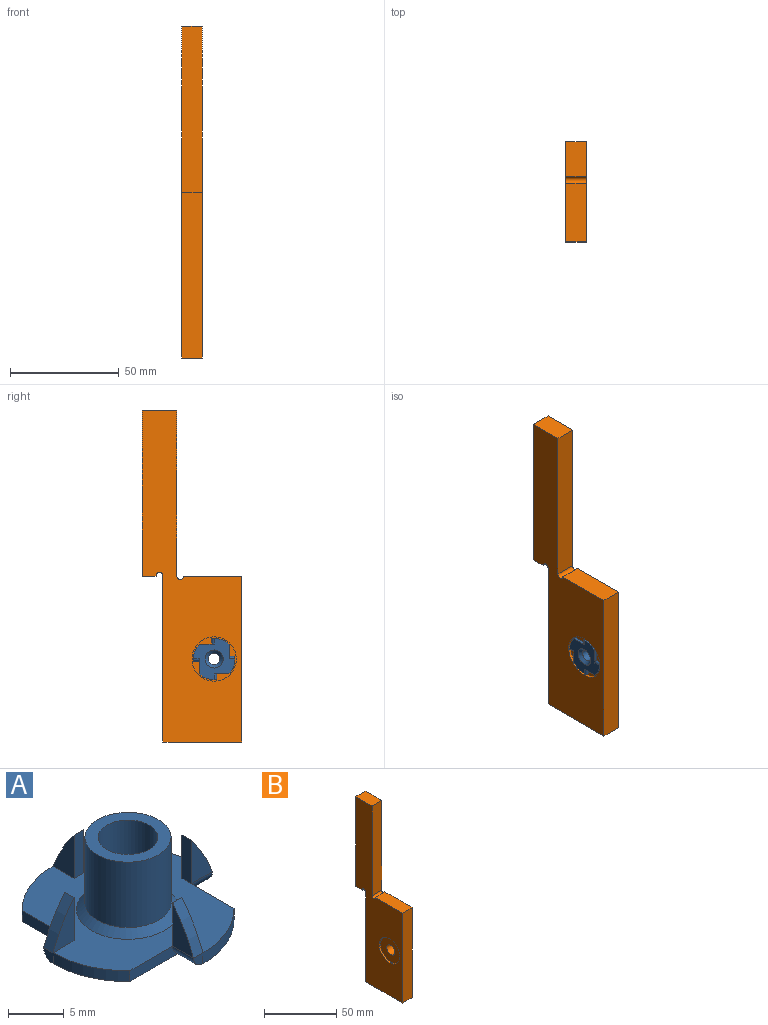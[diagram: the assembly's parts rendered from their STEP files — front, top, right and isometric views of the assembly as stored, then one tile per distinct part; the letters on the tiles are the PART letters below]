
ASSEMBLY  parts=2 mates=1
PART A: 39 faces, bbox 19.1x19.1x9.1 mm
  f0: cylinder r=9.53mm len=6.86mm, axis (0,0,-1), area 9.1mm2, adj f7,f10,f26,f28
  f1: cylinder r=16.73mm len=4.76mm, axis (0,-1,0), area 6.5mm2, adj f2,f3,f5,f6
  f2: plane 1.19x1.19mm, normal (1,0,0), area 1.1mm2, adj f1,f4,f27
  f3: plane 4.76x2.67mm, normal (0,-1,0), area 7.2mm2, adj f1,f4,f6
  f4: cylinder r=1.19mm len=2.67mm, axis (-1,0,0), area 5mm2, adj f2,f3,f7,f26
  f5: plane 4.76x2.67mm, normal (0,1,0), area 7.2mm2, adj f1,f6,f28
  f6: plane 4.76x1.19mm, normal (-1,0,0), area 5.7mm2, adj f1,f3,f5,f28
  f7: plane 6.61x1.19mm, normal (1,0,0), area 6.8mm2, adj f0,f4,f26,f28
  f8: cylinder r=9.53mm len=6.86mm, axis (0,0,-1), area 9.1mm2, adj f15,f18,f26,f28
  f9: cylinder r=16.73mm len=4.76mm, axis (-1,0,0), area 6.5mm2, adj f10,f11,f13,f14
  f10: plane 1.19x1.19mm, normal (0,-1,0), area 1.1mm2, adj f0,f9,f12
  f11: plane 4.76x2.67mm, normal (-1,0,0), area 7.2mm2, adj f9,f12,f14
  f12: cylinder r=1.19mm len=2.67mm, axis (0,1,0), area 5mm2, adj f10,f11,f15,f26
  f13: plane 4.76x2.67mm, normal (1,0,0), area 7.2mm2, adj f9,f14,f28
  f14: plane 4.76x1.19mm, normal (0,1,0), area 5.7mm2, adj f9,f11,f13,f28
  f15: plane 6.61x1.19mm, normal (0,-1,0), area 6.8mm2, adj f8,f12,f26,f28
  f16: cylinder r=9.53mm len=6.86mm, axis (0,0,-1), area 9.1mm2, adj f23,f26,f28,f34
  f17: cylinder r=16.73mm len=4.76mm, axis (0,1,0), area 6.5mm2, adj f18,f19,f21,f22
  f18: plane 1.19x1.19mm, normal (-1,0,0), area 1.1mm2, adj f8,f17,f20
  f19: plane 4.76x2.67mm, normal (0,1,0), area 7.2mm2, adj f17,f20,f22
  f20: cylinder r=1.19mm len=2.67mm, axis (1,0,0), area 5mm2, adj f18,f19,f23,f26
  f21: plane 4.76x2.67mm, normal (0,-1,0), area 7.2mm2, adj f17,f22,f28
  f22: plane 4.76x1.19mm, normal (1,0,0), area 5.7mm2, adj f17,f19,f21,f28
  f23: plane 6.61x1.19mm, normal (-1,0,0), area 6.8mm2, adj f16,f20,f26,f28
  f24: plane 4.76x2.67mm, normal (-1,0,0), area 7.2mm2, adj f28,f37,f38
  f25: cone r=2.68mm half-angle=45deg, axis (0,0,-1), area 44.3mm2, adj f26,f32
  f26: plane 19.05x19.05mm, normal (0,0,-1), area 182.6mm2, adj f0,f4,f7,f8,f12,f15,f16,f20
  f27: cylinder r=9.53mm len=6.86mm, axis (0,0,-1), area 9.1mm2, adj f2,f26,f28,f33
  f28: plane 19.05x19.05mm, normal (0,0,1), area 169mm2, adj f0,f5,f6,f7,f8,f13,f14,f15
  f29: cone r=4.64mm half-angle=45deg, axis (0,0,-1), area 28.8mm2, adj f28,f30
  f30: cylinder r=3.87mm len=7.75mm, axis (0,0,-1), area 174.9mm2, adj f29,f31
  f31: plane 7.75x7.75mm, normal (0,0,1), area 24.6mm2, adj f30,f32
  f32: cylinder r=2.68mm len=7.68mm, axis (0,0,-1), area 129.4mm2, adj f25,f31
  f33: plane 6.61x1.19mm, normal (0,1,0), area 6.8mm2, adj f26,f27,f28,f36
  f34: plane 1.19x1.19mm, normal (0,1,0), area 1.1mm2, adj f16,f36,f38
  f35: plane 4.76x2.67mm, normal (1,0,0), area 7.2mm2, adj f36,f37,f38
  f36: cylinder r=1.19mm len=2.67mm, axis (0,-1,0), area 5mm2, adj f26,f33,f34,f35
  f37: plane 4.76x1.19mm, normal (0,-1,0), area 5.7mm2, adj f24,f28,f35,f38
  f38: cylinder r=16.73mm len=4.76mm, axis (1,0,0), area 6.5mm2, adj f24,f34,f35,f37
PART B: 15 faces, bbox 9.5x45.7x152.4 mm
  f0: plane 9.53x6.35mm, normal (0,0,-1), area 60.5mm2, adj f2,f6,f9,f14
  f1: plane 26.67x9.53mm, normal (0,0,1), area 254mm2, adj f2,f3,f9,f13
  f2: plane 152.4x45.72mm, normal (-1,0,0), area 3635.5mm2, adj f0,f1,f3,f4,f5,f6,f7,f8
  f3: plane 76.2x9.53mm, normal (0,-1,0), area 725.8mm2, adj f1,f2,f4,f9
  f4: plane 36.2x9.53mm, normal (0,0,-1), area 344.8mm2, adj f2,f3,f5,f9
  f5: plane 76.2x9.53mm, normal (0,1,0), area 725.8mm2, adj f2,f4,f9,f14
  f6: plane 76.2x9.53mm, normal (0,1,0), area 725.8mm2, adj f0,f2,f7,f9
  f7: plane 15.88x9.53mm, normal (0,0,1), area 151.2mm2, adj f2,f6,f8,f9
  f8: plane 76.2x9.53mm, normal (0,-1,0), area 725.8mm2, adj f2,f7,f9,f13
  f9: plane 152.4x45.72mm, normal (1,0,0), area 3910.2mm2, adj f0,f1,f3,f4,f5,f6,f7,f8
  f10: cylinder r=3.98mm len=8.26mm, axis (-1,0,0), area 206.2mm2, adj f9,f11
  f11: plane 20.32x20.32mm, normal (-1,0,0), area 274.7mm2, adj f10,f12
  f12: cylinder r=10.16mm len=20.32mm, axis (-1,0,0), area 81.1mm2, adj f2,f11
  f13: cylinder r=1.59mm len=9.53mm, axis (-1,0,0), area 47.5mm2, adj f1,f2,f8,f9
  f14: cylinder r=1.59mm len=9.53mm, axis (-1,0,0), area 47.5mm2, adj f0,f2,f5,f9
PLACE A rot(axis=(-0.58,0.58,-0.58),120deg) t=(42.47,-33.62,-28.74)mm
PLACE B t=(42.39,-13.3,-76.37)mm
MATE fastened B.f10 <-> A.f0  axis (-1,0,0) through (43.66,-33.62,-28.74)mm
